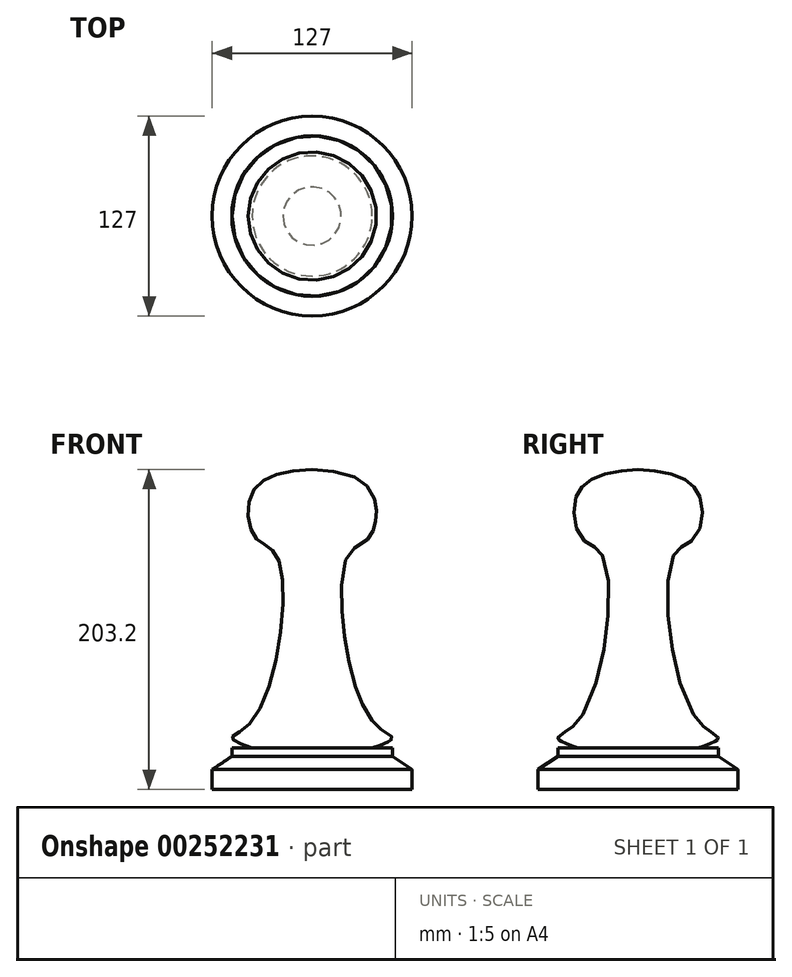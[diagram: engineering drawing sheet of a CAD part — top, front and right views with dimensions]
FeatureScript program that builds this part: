
annotation { "Feature Type Name" : "Feature", "Feature Type Description" : "" }
export const myFeature = defineFeature(function(context is Context, id is Id, definition is map)
    precondition{}
    {
        {
            var Q0;
            Q0=qCreatedBy(makeId("Front.planeOp"),FACE);
            var sketch = newSketch(context, id + "F0", { "sketchPlane" : qUnion([Q0])});
            skLineSegment(sketch, "E0", {"start": v(0, -101.56) * mm, "end": v(0, 101.64) * mm});
            skLineSegment(sketch, "E1", {"start": v(0, -101.56) * mm, "end": v(-63.5, -101.56) * mm});
            skLineSegment(sketch, "E2", {"start": v(-63.5, -101.56) * mm, "end": v(-63.5, -88.94) * mm});
            skLineSegment(sketch, "E3", {"start": v(-63.5, -88.94) * mm, "end": v(-50.98, -80.53) * mm});
            skLineSegment(sketch, "E4", {"start": v(-50.98, -80.53) * mm, "end": v(-50.98, -75.32) * mm});
            skLineSegment(sketch, "E5", {"start": v(-50.98, -75.32) * mm, "end": v(-38.14, -75.32) * mm});
            skFitSpline(sketch, "E6", {"points": [v(-38.14, -75.32) * mm, v(-50.91, -69) * mm, v(-36.41, -55.79) * mm, v(-21.83, 45.57) * mm, v(-35.85, 58.14) * mm, v(-38.14, 86.88) * mm, v(0, 101.64) * mm], "startDerivative": vector(-172.33, 63.52) * mm, "endDerivative": vector(295.43, 10.46) * mm});
            skLineSegment(sketch, "E7", {"start": v(0, -112.39) * mm, "end": v(0, 105.93) * mm, "construction": true});
            skSolve(sketch);
        }
        {
            var Q0;
            Q0=makeQuery(id+"F0.imprint","IMPRINT",FACE,{"disambiguationData":[TD([[makeQuery(id+"F0.imprint","IMPRINT",EDGE,{"derivedFrom":sQuery(id+"F0.wireOp",EDGE,"E0")}),1.0]])]});
            var Q1;
            Q1=sQuery(id+"F0.wireOp",EDGE,"E7");
            revolve(context, id + "F1", {"entities" : qUnion([Q0]), "axis" : qUnion([Q1]), "revolveType" : RevolveType.FULL});
        }
    });
